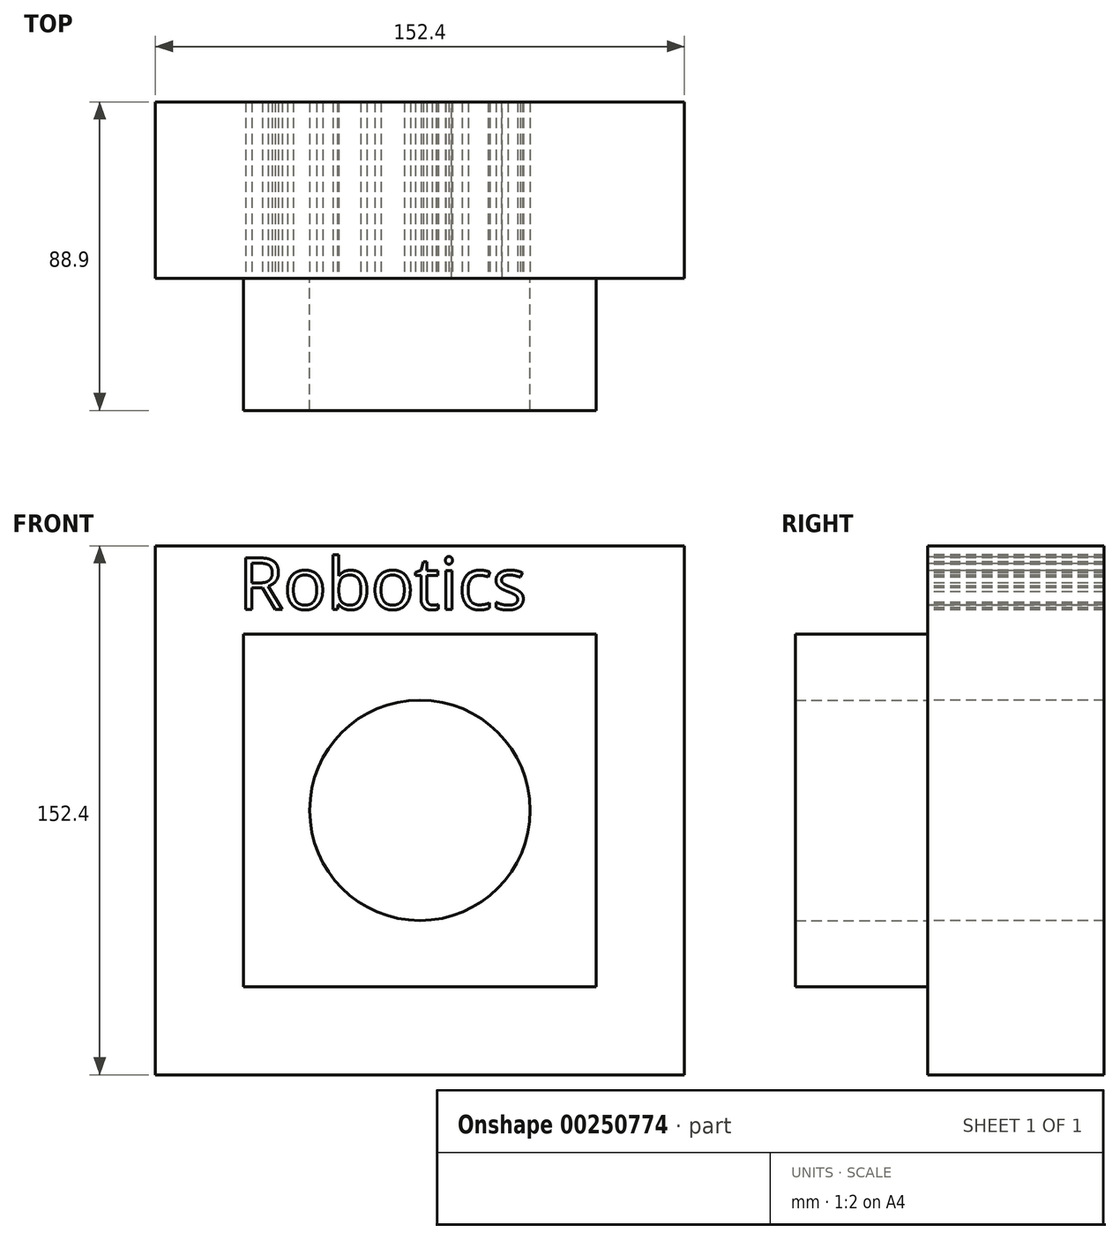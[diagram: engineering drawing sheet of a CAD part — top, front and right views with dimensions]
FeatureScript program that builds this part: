
annotation { "Feature Type Name" : "Feature", "Feature Type Description" : "" }
export const myFeature = defineFeature(function(context is Context, id is Id, definition is map)
    precondition{}
    {
        {
            var Q0;
            Q0=qCreatedBy(makeId("Front.planeOp"),FACE);
            var sketch = newSketch(context, id + "F0", { "sketchPlane" : qUnion([Q0])});
            skCircle(sketch, "E0", {"center": v(0, 0) * mm, "radius": 31.75 * mm});
            skLineSegment(sketch, "E1.bottom", {"start": v(50.8, 50.8) * mm, "end": v(-50.8, 50.8) * mm});
            skLineSegment(sketch, "E1.top", {"start": v(50.8, -50.8) * mm, "end": v(-50.8, -50.8) * mm});
            skLineSegment(sketch, "E1.left", {"start": v(50.8, 50.8) * mm, "end": v(50.8, -50.8) * mm});
            skLineSegment(sketch, "E1.right", {"start": v(-50.8, 50.8) * mm, "end": v(-50.8, -50.8) * mm});
            skLineSegment(sketch, "E2.bottom", {"start": v(-76.2, 76.2) * mm, "end": v(76.2, 76.2) * mm});
            skLineSegment(sketch, "E2.top", {"start": v(-76.2, -76.2) * mm, "end": v(76.2, -76.2) * mm});
            skLineSegment(sketch, "E2.left", {"start": v(-76.2, 76.2) * mm, "end": v(-76.2, -76.2) * mm});
            skLineSegment(sketch, "E2.right", {"start": v(76.2, 76.2) * mm, "end": v(76.2, -76.2) * mm});
            skSolve(sketch);
        }
        {
            var Q0;
            Q0=makeQuery(id+"F0.imprint","IMPRINT",FACE,{"disambiguationData":[TD([[makeQuery(id+"F0.imprint","IMPRINT",EDGE,{"derivedFrom":sQuery(id+"F0.wireOp",EDGE,"E0")}),-1.0]])]});
            extrude(context, id + "F1", {"entities" : qUnion([Q0]), "depth" : 38.1 * mm});
        }
        {
            var Q0;
            Q0=makeQuery(id+"F0.imprint","IMPRINT",FACE,{"disambiguationData":[TD([[makeQuery(id+"F0.imprint","IMPRINT",EDGE,{"derivedFrom":sQuery(id+"F0.wireOp",EDGE,"E1.bottom")}),-1.0]])]});
            var Q1;
            Q1=makeQuery(id+"F0.imprint","IMPRINT",FACE,{"disambiguationData":[TD([[makeQuery(id+"F0.imprint","IMPRINT",EDGE,{"derivedFrom":sQuery(id+"F0.wireOp",EDGE,"E0")}),-1.0]])]});
            extrude(context, id + "F2", {"entities" : qUnion([Q0, Q1]), "oppositeDirection" : true, "depth" : 50.8 * mm});
        }
        {
            var Q0;
            Q0=makeQuery(id+"F1.opExtrude","CAP_FACE",FACE,{"disambiguationData":[OSD([sQuery(id+"F0.wireOp",EDGE,"E0"),sQuery(id+"F0.wireOp",EDGE,"E1.bottom"),sQuery(id+"F0.wireOp",EDGE,"E1.top"),sQuery(id+"F0.wireOp",EDGE,"E1.left"),sQuery(id+"F0.wireOp",EDGE,"E1.right")])],"isStart":false});
            var sketch = newSketch(context, id + "F3", { "sketchPlane" : qUnion([Q0])});
            skText(sketch, "E3", { "text": "Robotics\n", "fontName": "OpenSans-Regular.ttf"});
            const initialGuessF3  = {"E3": [-0.05217, 0.05789, 1, 0, 0.01493]};
            skSetInitialGuess(sketch, initialGuessF3);
            skSolve(sketch);
        }
        {
            var Q0;
            Q0 = qSketchRegion(id + "F3", true);
            extrude(context, id + "F4", {"entities" : qUnion([Q0]), "operationType" : NewBodyOperationType.REMOVE, "endBound" : BoundingType.THROUGH_ALL, "oppositeDirection" : true, "depth" : 81.53 * mm});
        }
    });
